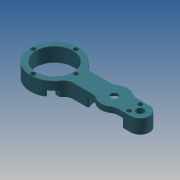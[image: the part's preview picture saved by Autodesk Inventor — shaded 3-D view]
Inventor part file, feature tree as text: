
AUTODESK INVENTOR PART (.ipt)
format: ipt  version: 2013 (Build 170138000, 138)  size: 332,288 bytes
history: native  units: mm
features: extrude x18, sketch x18, pattern_circular x2, fillet x2, projected_geometry x2, mirror x1
ambient origin geometry x8: Origin, YZ Plane, XZ Plane, XY Plane, X Axis, Y Axis, Z Axis, Center Point
bodies: Solid1 (feature_tree)
feature tree (43):
  extrude  "Extrusion1"  Depth=12.5mm
  extrude  "Extrusion2"  Depth=38.0mm TaperAngle=0.0deg
  extrude  "Extrusion3"  Depth=35.0mm
  extrude  "Extrusion4"  Depth=35.0mm TaperAngle=0.0deg
  extrude  "Extrusion5"  Depth=23.0mm TaperAngle=0.0deg
  mirror  "Mirror1"
  extrude  "Extrusion6"  Depth=4.0mm TaperAngle=0.0deg
  extrude  "Extrusion7"  Depth=4.0mm TaperAngle=0.0deg
  extrude  "Extrusion9"  Depth=7.5mm
  extrude  "Extrusion10"  Depth=7.5mm
  extrude  "Extrusion11"  Depth=3.0mm TaperAngle=0.0deg
  extrude  "Extrusion12"  Depth=1.0mm
  extrude  "Extrusion13"  Depth=1.5mm TaperAngle=0.0deg
  extrude  "Extrusion14"  Depth=7.5mm
  extrude  "Extrusion17"  Depth=1.5mm TaperAngle=0.0deg
  extrude  "Extrusion18"  Depth=5.0mm TaperAngle=0.0deg
  pattern_circular  "Circular Pattern2"  [2 undecoded]
  extrude  "Extrusion20"  Depth=3.5mm
  fillet  "Fillet1"  Radius=7.0mm
  fillet  "Fillet2"  Radius=40.0mm
  extrude  "Extrusion21"  Depth=4.0mm TaperAngle=0.0deg
  pattern_circular  "Circular Pattern3"  [2 undecoded]
  extrude  "Extrusion22"  Depth=12.5mm
  sketch  "Sketch1"  dims[d0=115.5mm d2=12.5mm]
  sketch  "Sketch2"  dims[d3=12.0mm d4=38.0mm d5=0.0mm]
  sketch  "Sketch3"  dims[d6=44.563422mm d8=35.0mm]
  sketch  "Sketch4"  dims[d9=10.0mm d10=35.0mm d11=0.0mm]
  sketch  "Sketch5"  dims[d12=50.0mm d14=23.0mm d15=0.0mm]
  sketch  "Sketch6"  dims[d16=21.0mm d19=4.0mm d20=0.0mm]
  projected_geometry  "Projected Loop1"
  sketch  "Sketch7"  dims[d22=7.5mm d23=4.0mm d24=0.0mm]
  sketch  "Sketch9"  dims[d25=3.0mm d27=7.5mm]
  sketch  "Sketch10"  dims[d28=7.5mm d29=7.5mm]
  sketch  "Sketch11"  dims[d30=7.5mm d31=3.0mm d32=0.0mm]
  sketch  "Sketch12"  dims[d36=4.0mm d37=0.0mm d43=1.0mm]
  sketch  "Sketch13"  dims[d44=1.5mm d45=0.0mm d46=1.5mm d47=0.0mm]
  sketch  "Sketch14"  dims[d50=65.0mm d51=7.5mm]
  sketch  "Sketch17"  dims[d52=1.5mm d53=0.0mm d54=1.5mm d55=0.0mm]
  sketch  "Sketch18"  dims[d56=11.4mm d57=0.0mm d58=5.0mm d59=0.0mm]
  sketch  "Sketch20"  dims[d68=44.055422mm]
  sketch  "Sketch21"  dims[d71=7.0mm d72=0.0mm]
  sketch  "Sketch22"  dims[d73=28.75mm d74=22.5mm d75=3.5mm d76=7.0mm d77=0.0mm d83=40.0mm d84=360.0deg d88=4.0mm d89=0.0mm d90=2.0mm d91=12.5mm d92=5.5mm d93=10.0mm d94=0.0mm d95=5.5mm d96=40.0mm d97=360.0deg d99=1.0mm d100=1.0mm d101=0.0mm]
  projected_geometry  "Project Cut Edges1"
note: 4 required parameter values undecoded (feature->parameter linkage not recoverable at this tier; creation-order binding heuristic only, values carry confidence <= 0.55)
